# Revit family: Cabinet_Accessories-Danver-Tall_Side_Panel
name_source: partatom
category: Casework
units: mm (PartAtom-declared; Revit-internal decimal feet)

## family parameters
Always vertical = Yes
Cut with Voids When Loaded = No
Room Calculation Point = No
Shared = No
Work Plane-Based = No

## types (6) — shared parameters
Base Cab Depth = 2' - 0"
Construction Type = Type 304 Stainless Steel
Default Elevation = 0"
Door Style = Door : Hampton
Handle Material = Metal - Danver - Chrome Plated Steel
Keynote = 12 35 28
Manufacturer = Danver Outdoor Kitchens
Panel Material = Metal - Danver - Stainless Steel
Panel Thickness = 3/4"
Product Documentation Link = https://danver.com
Product Page URL = https://danver.com
Threshold Offset = 1 1/4"
Toe Kick Length = 1' - 10 3/4"
Toe Kick Material = Metal - Danver - Toe Kick
URL = www.danver.com
Version = 2019 - V1.0B

## per-type parameters (varying)
| type | Description | Model | Panel Height | Panel Width |
| 24.88 Inch Width - 84 Inch Height | 24.88"x84" Tall Side Panel | OSPT 2484 | 6' - 7 1/2" | 2' - 0 7/8" |
| 24 Inch Width - 84 Inch Height | 24"x84" Tall Side Panel | OFET 2484 | 6' - 7 1/2" | 2' - 0" |
| 24.88 Inch Width - 90 Inch Height | 24.88"x90" Tall Side Panel | OSPT 2490 | 7' - 1 1/2" | 2' - 0 7/8" |
| 24 Inch Width - 90 Inch Height | 24"x90" Tall Side Panel | OFET 2490 | 7' - 1 1/2" | 2' - 0" |
| 24.88 Inch Width - 96 Inch Height | 24.88"x96" Tall Side Panel | OSPT 2496 | 7' - 7 1/2" | 2' - 0 7/8" |
| 24 Inch Width - 96 Inch Height | 24"x96" Tall Side Panel | OFET 2496 | 7' - 7 1/2" | 2' - 0" |

## geometry (parser evidence)
native form markers: Sweep x15
no freeform markers — native parametric forms only
